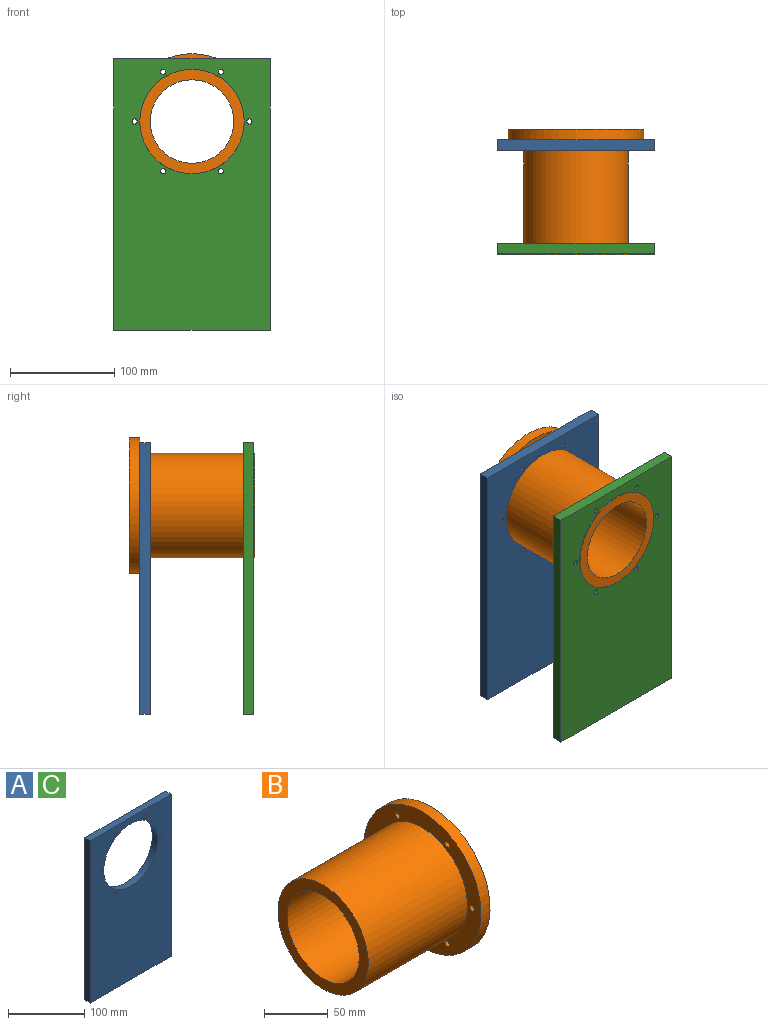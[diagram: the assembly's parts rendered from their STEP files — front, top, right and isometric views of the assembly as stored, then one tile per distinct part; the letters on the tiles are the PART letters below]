
ASSEMBLY  parts=3 mates=3
PART A: 13 faces, bbox 150x10x260 mm
  f0: plane 150x10mm, normal (0,0,1), area 1500mm2, adj f1,f4,f5,f6
  f1: plane 260x10mm, normal (-1,0,0), area 2600mm2, adj f0,f2,f5,f6
  f2: plane 150x10mm, normal (0,0,-1), area 1500mm2, adj f1,f4,f5,f6
  f3: cylinder r=50mm len=100mm, axis (0,1,0), area 3141.6mm2, adj f5,f6
  f4: plane 260x10mm, normal (1,0,0), area 2600mm2, adj f0,f2,f5,f6
  f5: plane 260x150mm, normal (0,-1,0), area 31028.2mm2, adj f0,f1,f2,f3,f4,f7,f8,f9
  f6: plane 260x150mm, normal (0,1,0), area 31028.2mm2, adj f0,f1,f2,f3,f4,f7,f8,f9
  f7: cylinder r=2.5mm len=10mm, axis (0,-1,0), area 157.1mm2, adj f5,f6
  f8: cylinder r=2.5mm len=10mm, axis (0,-1,0), area 157.1mm2, adj f5,f6
  f9: cylinder r=2.5mm len=10mm, axis (0,-1,0), area 157.1mm2, adj f5,f6
  f10: cylinder r=2.5mm len=10mm, axis (0,-1,0), area 157.1mm2, adj f5,f6
  f11: cylinder r=2.5mm len=10mm, axis (0,-1,0), area 157.1mm2, adj f5,f6
  f12: cylinder r=2.5mm len=10mm, axis (0,-1,0), area 157.1mm2, adj f5,f6
PART B: 24 faces, bbox 120x130x130 mm
  f0: cylinder r=50mm len=110mm, axis (-1,0,0), area 34557.5mm2, adj f1,f5
  f1: plane 100x100mm, normal (-1,0,0), area 2827.4mm2, adj f0,f2
  f2: cylinder r=40mm len=120mm, axis (-1,0,0), area 30159.3mm2, adj f1,f3
  f3: plane 130x130mm, normal (1,0,0), area 7650.3mm2, adj f2,f4,f8,f11,f14,f17,f20,f23
  f4: cylinder r=65mm len=130mm, axis (-1,0,0), area 4084.1mm2, adj f3,f5
  f5: plane 130x130mm, normal (-1,0,0), area 5301.4mm2, adj f0,f4,f6,f9,f12,f15,f18,f21
  f6: cylinder r=2.5mm len=5mm, axis (1,0,0), area 62.8mm2, adj f5,f7
  f7: plane 11.25x11.25mm, normal (1,0,0), area 79.8mm2, adj f6,f8
  f8: cylinder r=5.62mm len=11.25mm, axis (1,0,0), area 212.1mm2, adj f3,f7
  f9: cylinder r=2.5mm len=5mm, axis (1,0,0), area 62.8mm2, adj f5,f10
  f10: plane 11.25x11.25mm, normal (1,0,0), area 79.8mm2, adj f9,f11
  f11: cylinder r=5.62mm len=11.25mm, axis (1,0,0), area 212.1mm2, adj f3,f10
  f12: cylinder r=2.5mm len=5mm, axis (1,0,0), area 62.8mm2, adj f5,f13
  f13: plane 11.25x11.25mm, normal (1,0,0), area 79.8mm2, adj f12,f14
  f14: cylinder r=5.62mm len=11.25mm, axis (1,0,0), area 212.1mm2, adj f3,f13
  f15: cylinder r=2.5mm len=5mm, axis (1,0,0), area 62.8mm2, adj f5,f16
  f16: plane 11.25x11.25mm, normal (1,0,0), area 79.8mm2, adj f15,f17
  f17: cylinder r=5.62mm len=11.25mm, axis (1,0,0), area 212.1mm2, adj f3,f16
  f18: cylinder r=2.5mm len=5mm, axis (1,0,0), area 62.8mm2, adj f5,f19
  f19: plane 11.25x11.25mm, normal (1,0,0), area 79.8mm2, adj f18,f20
  f20: cylinder r=5.62mm len=11.25mm, axis (1,0,0), area 212.1mm2, adj f3,f19
  f21: cylinder r=2.5mm len=5mm, axis (1,0,0), area 62.8mm2, adj f5,f22
  f22: plane 11.25x11.25mm, normal (1,0,0), area 79.8mm2, adj f21,f23
  f23: cylinder r=5.62mm len=11.25mm, axis (1,0,0), area 212.1mm2, adj f3,f22
PART C: same geometry as A
PLACE A at identity fixed
PLACE B rot(axis=(0,0,1),90deg) t=(0,-110,200)mm
PLACE C t=(0,-99.24,0)mm
MATE planar C.f4 <-> A.f4  axis (1,0,0) through (75,-104.24,130)mm
MATE fastened B.f21 <-> A.f9  axis (0,-1,0) through (55,0,200)mm
MATE planar C.f0 <-> A.f0  axis (0,0,1) through (75,-109.24,260)mm
